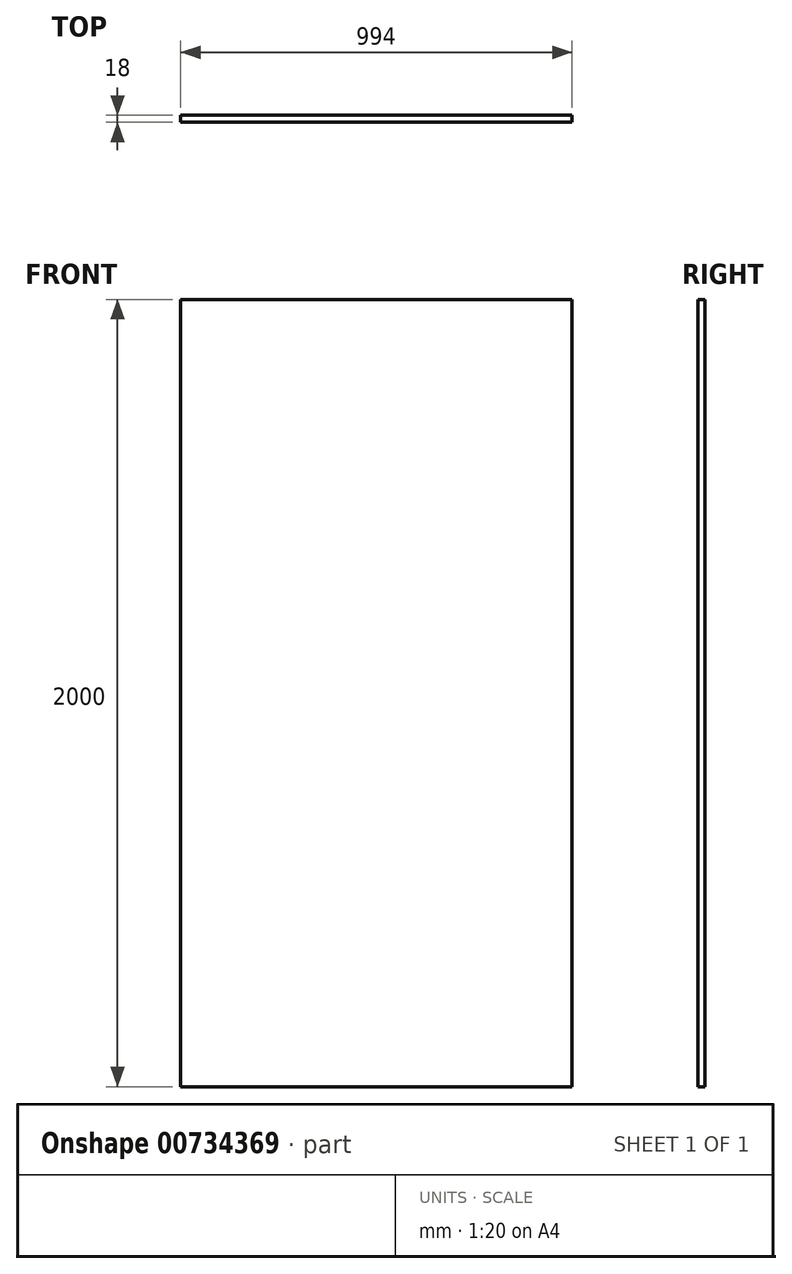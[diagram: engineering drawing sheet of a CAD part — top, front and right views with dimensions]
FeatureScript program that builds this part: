
annotation { "Feature Type Name" : "Feature", "Feature Type Description" : "" }
export const myFeature = defineFeature(function(context is Context, id is Id, definition is map)
    precondition{}
    {
        {
            var Q0;
            Q0=qCreatedBy(makeId("Front.planeOp"),FACE);
            var sketch = newSketch(context, id + "F0", { "sketchPlane" : qUnion([Q0])});
            skLineSegment(sketch, "E0.bottom", {"start": v(-497, -1000) * mm, "end": v(497, -1000) * mm});
            skLineSegment(sketch, "E0.top", {"start": v(-497, 1000) * mm, "end": v(497, 1000) * mm});
            skLineSegment(sketch, "E0.left", {"start": v(-497, -1000) * mm, "end": v(-497, 1000) * mm});
            skLineSegment(sketch, "E0.right", {"start": v(497, -1000) * mm, "end": v(497, 1000) * mm});
            skPoint(sketch, "E0.middle", {"position": v(0, 0) * mm});
            skSolve(sketch);
        }
        {
            var Q0;
            Q0 = qSketchRegion(id + "F0", true);
            extrude(context, id + "F1", {"entities" : qUnion([Q0]), "oppositeDirection" : true, "depth" : 18 * mm, "offsetDistance" : 25 * mm});
        }
    });
